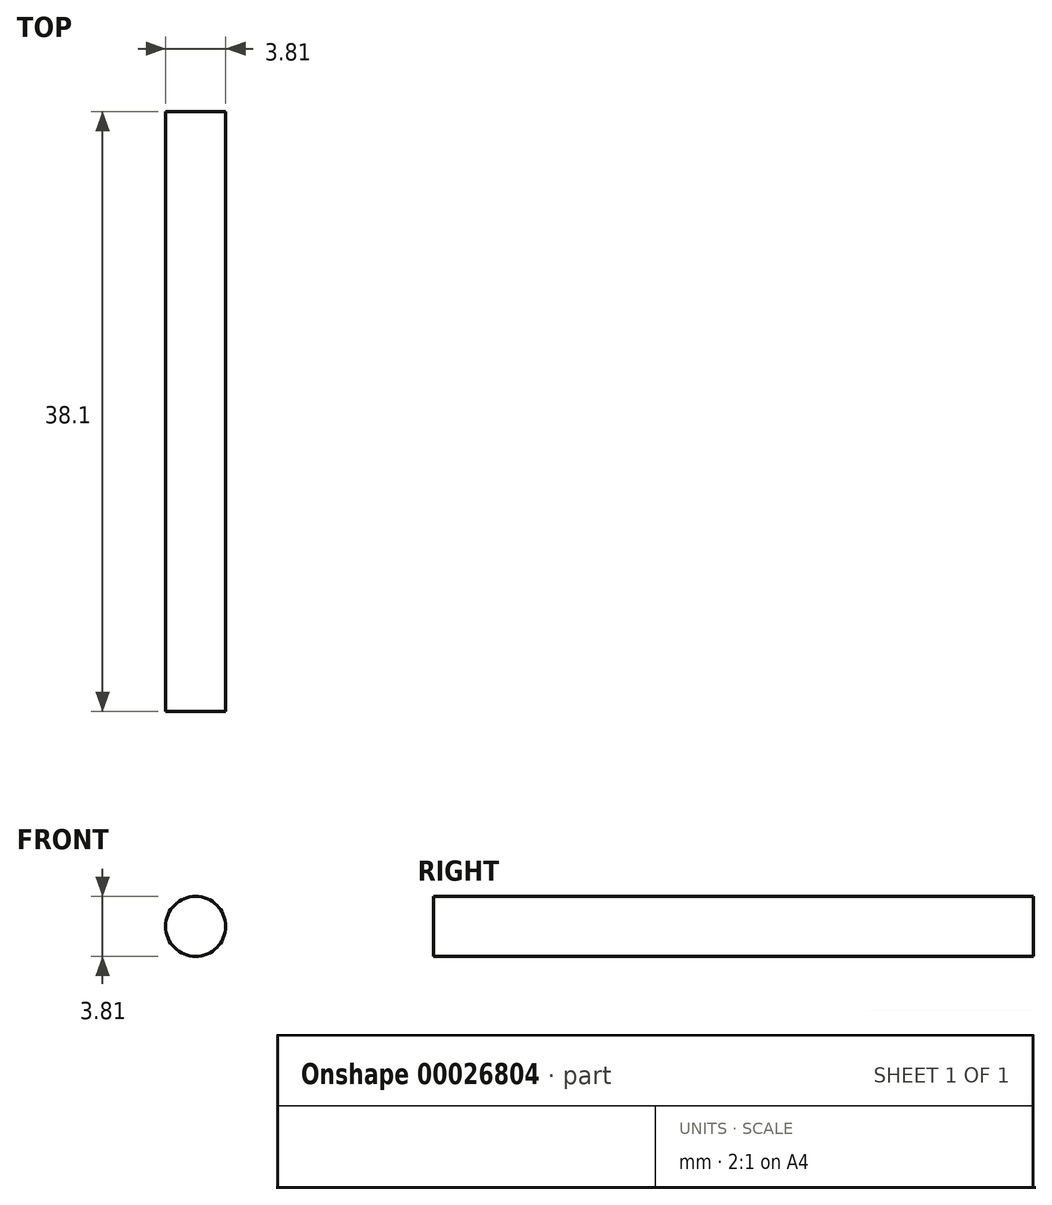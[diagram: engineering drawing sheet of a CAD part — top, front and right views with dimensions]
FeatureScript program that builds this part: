
annotation { "Feature Type Name" : "Feature", "Feature Type Description" : "" }
export const myFeature = defineFeature(function(context is Context, id is Id, definition is map)
    precondition{}
    {
        {
            var Q0;
            Q0=qCreatedBy(makeId("Front.planeOp"),FACE);
            var sketch = newSketch(context, id + "F0", { "sketchPlane" : qUnion([Q0])});
            skCircle(sketch, "E0", {"center": v(32.48, 36.5) * mm, "radius": 1.9 * mm});
            skSolve(sketch);
        }
        {
            var Q0;
            Q0=makeQuery(id+"F0.imprint","IMPRINT",FACE,{"disambiguationData":[TD([[makeQuery(id+"F0.imprint","IMPRINT",EDGE,{"derivedFrom":sQuery(id+"F0.wireOp",EDGE,"E0")}),1.0]])]});
            extrude(context, id + "F1", {"entities" : qUnion([Q0]), "depth" : 38.1 * mm});
        }
    });
